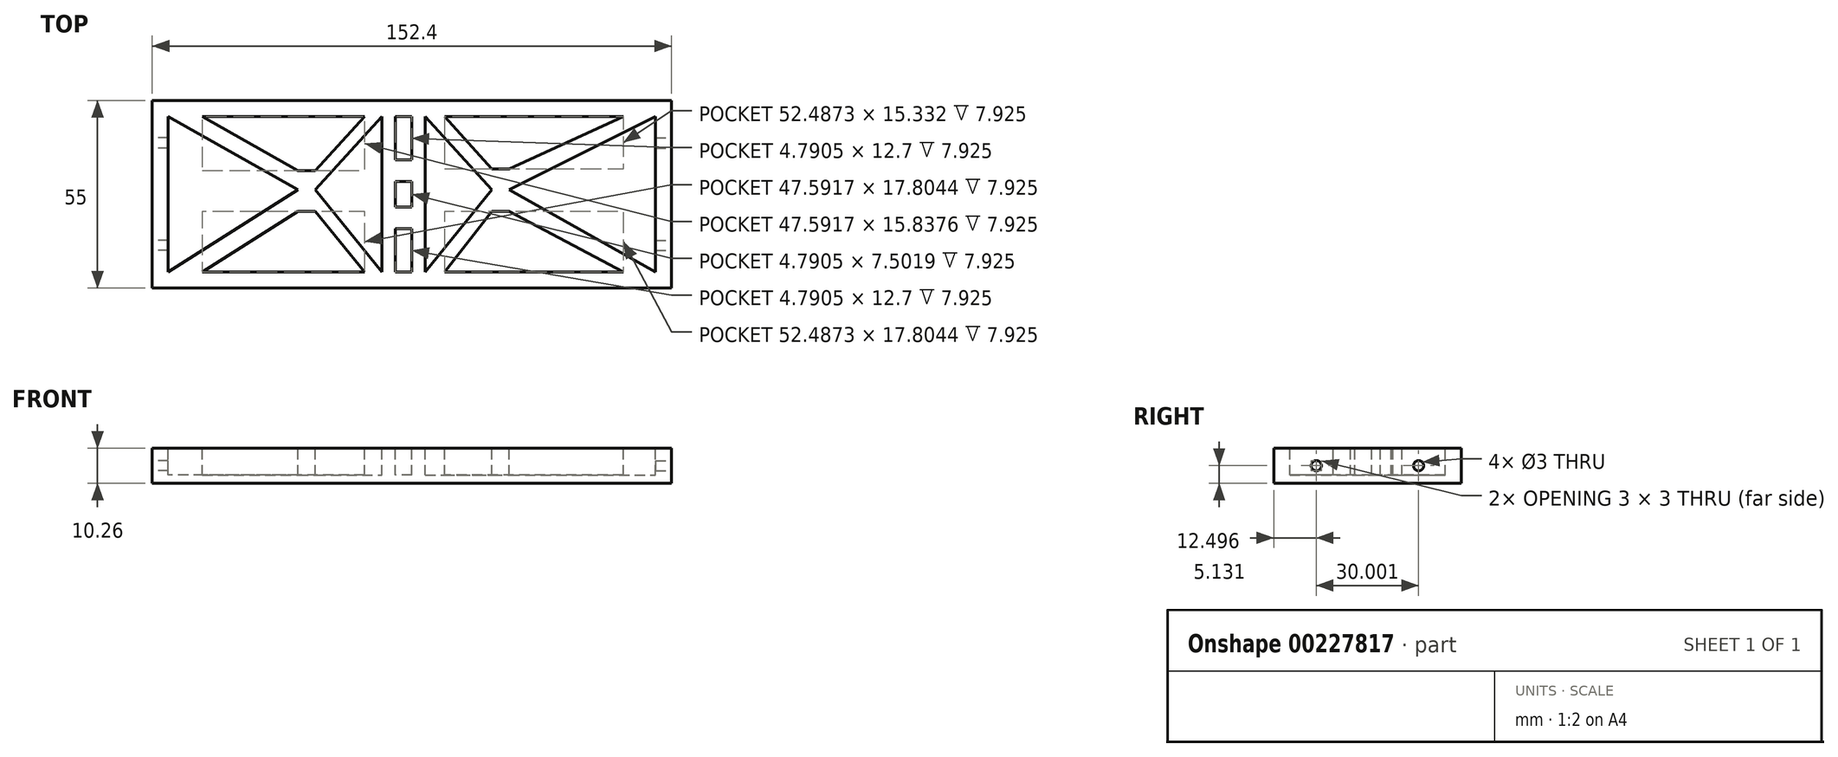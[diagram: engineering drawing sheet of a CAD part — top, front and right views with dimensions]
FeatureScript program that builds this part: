
annotation { "Feature Type Name" : "Feature", "Feature Type Description" : "" }
export const myFeature = defineFeature(function(context is Context, id is Id, definition is map)
    precondition{}
    {
        {
            var Q0;
            Q0=qCreatedBy(makeId("Top.planeOp"),FACE);
            var sketch = newSketch(context, id + "F0", { "sketchPlane" : qUnion([Q0])});
            skLineSegment(sketch, "E0.bottom", {"start": v(-61.95, 32.5) * mm, "end": v(90.45, 32.5) * mm});
            skLineSegment(sketch, "E0.top", {"start": v(-61.95, -22.5) * mm, "end": v(90.45, -22.5) * mm});
            skLineSegment(sketch, "E0.left", {"start": v(-61.95, 32.5) * mm, "end": v(-61.95, -22.5) * mm});
            skLineSegment(sketch, "E0.right", {"start": v(90.45, 32.5) * mm, "end": v(90.45, -22.5) * mm});
            skSolve(sketch);
        }
        {
            var Q0;
            Q0=makeQuery(id+"F0.imprint","IMPRINT",FACE,{"disambiguationData":[TD([[makeQuery(id+"F0.imprint","IMPRINT",EDGE,{"derivedFrom":sQuery(id+"F0.wireOp",EDGE,"E0.bottom")}),-1.0]])]});
            extrude(context, id + "F1", {"entities" : qUnion([Q0]), "depth" : 10.26 * mm});
        }
        {
            var Q0;
            Q0=makeQuery(id+"F1.opExtrude","CAP_FACE",FACE,{"disambiguationData":[OSD([sQuery(id+"F0.wireOp",EDGE,"E0.bottom"),sQuery(id+"F0.wireOp",EDGE,"E0.top"),sQuery(id+"F0.wireOp",EDGE,"E0.left"),sQuery(id+"F0.wireOp",EDGE,"E0.right")])],"isStart":false});
            var sketch = newSketch(context, id + "F2", { "sketchPlane" : qUnion([Q0])});
            skLineSegment(sketch, "E1", {"start": v(-57.25, -17.8) * mm, "end": v(-57.25, 27.8) * mm});
            skLineSegment(sketch, "E2", {"start": v(-57.25, 27.8) * mm, "end": v(-19.15, 6.28) * mm});
            skLineSegment(sketch, "E3", {"start": v(-19.15, 6.28) * mm, "end": v(-57.25, -17.8) * mm});
            skLineSegment(sketch, "E4", {"start": v(42.86, 6.28) * mm, "end": v(85.75, 27.8) * mm});
            skLineSegment(sketch, "E5", {"start": v(85.75, 27.8) * mm, "end": v(85.75, -17.8) * mm});
            skLineSegment(sketch, "E6", {"start": v(85.75, -17.8) * mm, "end": v(42.86, 6.28) * mm});
            skLineSegment(sketch, "E7", {"start": v(-14.07, 6.28) * mm, "end": v(5.5, 27.8) * mm});
            skLineSegment(sketch, "E8", {"start": v(5.5, 27.8) * mm, "end": v(5.5, -17.8) * mm});
            skLineSegment(sketch, "E9", {"start": v(5.5, -17.8) * mm, "end": v(-14.07, 6.28) * mm});
            skLineSegment(sketch, "E10", {"start": v(37.78, 6.28) * mm, "end": v(18.2, 27.8) * mm});
            skLineSegment(sketch, "E11", {"start": v(18.2, 27.8) * mm, "end": v(18.2, -17.8) * mm});
            skLineSegment(sketch, "E12", {"start": v(18.2, -17.8) * mm, "end": v(37.78, 6.28) * mm});
            skLineSegment(sketch, "E13", {"start": v(-47.2, -17.8) * mm, "end": v(-19.15, 0) * mm});
            skLineSegment(sketch, "E14", {"start": v(-19.15, 0) * mm, "end": v(-14.07, 0) * mm});
            skLineSegment(sketch, "E15", {"start": v(-14.07, 0) * mm, "end": v(0.4, -17.8) * mm});
            skLineSegment(sketch, "E16", {"start": v(0.4, -17.8) * mm, "end": v(-47.2, -17.8) * mm});
            skLineSegment(sketch, "E17", {"start": v(-47.2, 27.8) * mm, "end": v(-19.15, 11.96) * mm});
            skLineSegment(sketch, "E18", {"start": v(-19.15, 11.96) * mm, "end": v(-14.07, 11.96) * mm});
            skLineSegment(sketch, "E19", {"start": v(-14.07, 11.96) * mm, "end": v(0.4, 27.8) * mm});
            skLineSegment(sketch, "E20", {"start": v(0.4, 27.8) * mm, "end": v(-47.2, 27.8) * mm});
            skLineSegment(sketch, "E21", {"start": v(76.31, -17.8) * mm, "end": v(42.86, 0) * mm});
            skLineSegment(sketch, "E22", {"start": v(42.86, 0) * mm, "end": v(37.78, 0) * mm});
            skLineSegment(sketch, "E23", {"start": v(37.78, 0) * mm, "end": v(23.83, -17.8) * mm});
            skLineSegment(sketch, "E24", {"start": v(23.83, -17.8) * mm, "end": v(76.31, -17.8) * mm});
            skLineSegment(sketch, "E25", {"start": v(76.31, 27.8) * mm, "end": v(23.83, 27.8) * mm});
            skLineSegment(sketch, "E26", {"start": v(23.83, 27.8) * mm, "end": v(37.78, 12.47) * mm});
            skLineSegment(sketch, "E27", {"start": v(37.78, 12.47) * mm, "end": v(42.86, 12.47) * mm});
            skLineSegment(sketch, "E28", {"start": v(42.86, 12.47) * mm, "end": v(76.31, 27.8) * mm});
            skLineSegment(sketch, "E29.bottom", {"start": v(14.24, 27.8) * mm, "end": v(9.45, 27.8) * mm});
            skLineSegment(sketch, "E29.top", {"start": v(14.24, 15.1) * mm, "end": v(9.45, 15.1) * mm});
            skLineSegment(sketch, "E29.left", {"start": v(14.24, 27.8) * mm, "end": v(14.24, 15.1) * mm});
            skLineSegment(sketch, "E29.right", {"start": v(9.45, 27.8) * mm, "end": v(9.45, 15.1) * mm});
            skLineSegment(sketch, "E30.bottom", {"start": v(9.45, -5.1) * mm, "end": v(14.24, -5.1) * mm});
            skLineSegment(sketch, "E30.top", {"start": v(9.45, -17.8) * mm, "end": v(14.24, -17.8) * mm});
            skLineSegment(sketch, "E30.left", {"start": v(9.45, -5.1) * mm, "end": v(9.45, -17.8) * mm});
            skLineSegment(sketch, "E30.right", {"start": v(14.24, -5.1) * mm, "end": v(14.24, -17.8) * mm});
            skLineSegment(sketch, "E31.bottom", {"start": v(9.45, 1.25) * mm, "end": v(14.24, 1.25) * mm});
            skLineSegment(sketch, "E31.top", {"start": v(9.45, 8.75) * mm, "end": v(14.24, 8.75) * mm});
            skLineSegment(sketch, "E31.left", {"start": v(9.45, 1.25) * mm, "end": v(9.45, 8.75) * mm});
            skLineSegment(sketch, "E31.right", {"start": v(14.24, 1.25) * mm, "end": v(14.24, 8.75) * mm});
            skSolve(sketch);
        }
        {
            var Q0;
            Q0=makeQuery(id+"F2.imprint","IMPRINT",FACE,{"disambiguationData":[TD([[makeQuery(id+"F2.imprint","IMPRINT",EDGE,{"derivedFrom":sQuery(id+"F2.wireOp",EDGE,"E1")}),-1.0]])]});
            var Q1;
            Q1=makeQuery(id+"F2.imprint","IMPRINT",FACE,{"disambiguationData":[TD([[makeQuery(id+"F2.imprint","IMPRINT",EDGE,{"derivedFrom":sQuery(id+"F2.wireOp",EDGE,"E17")}),1.0]])]});
            var Q2;
            Q2=makeQuery(id+"F2.imprint","IMPRINT",FACE,{"disambiguationData":[TD([[makeQuery(id+"F2.imprint","IMPRINT",EDGE,{"derivedFrom":sQuery(id+"F2.wireOp",EDGE,"E13")}),-1.0]])]});
            var Q3;
            Q3=makeQuery(id+"F2.imprint","IMPRINT",FACE,{"disambiguationData":[TD([[makeQuery(id+"F2.imprint","IMPRINT",EDGE,{"derivedFrom":sQuery(id+"F2.wireOp",EDGE,"E7")}),-1.0]])]});
            var Q4;
            Q4=makeQuery(id+"F2.imprint","IMPRINT",FACE,{"disambiguationData":[TD([[makeQuery(id+"F2.imprint","IMPRINT",EDGE,{"derivedFrom":sQuery(id+"F2.wireOp",EDGE,"E29.bottom")}),1.0]])]});
            var Q5;
            Q5=makeQuery(id+"F2.imprint","IMPRINT",FACE,{"disambiguationData":[TD([[makeQuery(id+"F2.imprint","IMPRINT",EDGE,{"derivedFrom":sQuery(id+"F2.wireOp",EDGE,"E31.bottom")}),1.0]])]});
            var Q6;
            Q6=makeQuery(id+"F2.imprint","IMPRINT",FACE,{"disambiguationData":[TD([[makeQuery(id+"F2.imprint","IMPRINT",EDGE,{"derivedFrom":sQuery(id+"F2.wireOp",EDGE,"E30.bottom")}),-1.0]])]});
            var Q7;
            Q7=makeQuery(id+"F2.imprint","IMPRINT",FACE,{"disambiguationData":[TD([[makeQuery(id+"F2.imprint","IMPRINT",EDGE,{"derivedFrom":sQuery(id+"F2.wireOp",EDGE,"E10")}),1.0]])]});
            var Q8;
            Q8=makeQuery(id+"F2.imprint","IMPRINT",FACE,{"disambiguationData":[TD([[makeQuery(id+"F2.imprint","IMPRINT",EDGE,{"derivedFrom":sQuery(id+"F2.wireOp",EDGE,"E21")}),1.0]])]});
            var Q9;
            Q9=makeQuery(id+"F2.imprint","IMPRINT",FACE,{"disambiguationData":[TD([[makeQuery(id+"F2.imprint","IMPRINT",EDGE,{"derivedFrom":sQuery(id+"F2.wireOp",EDGE,"E4")}),-1.0]])]});
            var Q10;
            Q10=makeQuery(id+"F2.imprint","IMPRINT",FACE,{"disambiguationData":[TD([[makeQuery(id+"F2.imprint","IMPRINT",EDGE,{"derivedFrom":sQuery(id+"F2.wireOp",EDGE,"E25")}),1.0]])]});
            extrude(context, id + "F3", {"entities" : qUnion([Q0, Q1, Q2, Q3, Q4, Q5, Q6, Q7, Q8, Q9, Q10]), "operationType" : NewBodyOperationType.REMOVE, "oppositeDirection" : true, "depth" : 7.92 * mm});
        }
        {
            var Q0;
            Q0=makeQuery(id+"F1.opExtrude","SWEPT_FACE",FACE,{"disambiguationData":[OSD([sQuery(id+"F0.wireOp",EDGE,"E0.left")])]});
            var sketch = newSketch(context, id + "F4", { "sketchPlane" : qUnion([Q0])});
            skCircle(sketch, "E32", {"center": v(-20, 5.13) * mm, "radius": 1.5 * mm});
            skPoint(sketch, "E32.centerSnap0", {"position": v(-32.5, 5.13) * mm});
            skCircle(sketch, "E33", {"center": v(10, 5.13) * mm, "radius": 1.5 * mm});
            skPoint(sketch, "E33.centerSnap0", {"position": v(22.5, 5.13) * mm});
            skSolve(sketch);
        }
        {
            var Q0;
            Q0=makeQuery(id+"F1.opExtrude","SWEPT_FACE",FACE,{"disambiguationData":[OSD([sQuery(id+"F0.wireOp",EDGE,"E0.right")])]});
            var sketch = newSketch(context, id + "F5", { "sketchPlane" : qUnion([Q0])});
            skCircle(sketch, "E34", {"center": v(20, 5.13) * mm, "radius": 1.5 * mm});
            skPoint(sketch, "E34.centerSnap0", {"position": v(32.5, 5.13) * mm});
            skCircle(sketch, "E35", {"center": v(-10, 5.13) * mm, "radius": 1.5 * mm});
            skPoint(sketch, "E35.centerSnap0", {"position": v(-22.5, 5.13) * mm});
            skSolve(sketch);
        }
        {
            var Q0;
            Q0=makeQuery(id+"F5.imprint","IMPRINT",FACE,{"disambiguationData":[TD([[makeQuery(id+"F5.imprint","IMPRINT",EDGE,{"derivedFrom":sQuery(id+"F5.wireOp",EDGE,"E34")}),1.0]])]});
            var Q1;
            Q1=makeQuery(id+"F5.imprint","IMPRINT",FACE,{"disambiguationData":[TD([[makeQuery(id+"F5.imprint","IMPRINT",EDGE,{"derivedFrom":sQuery(id+"F5.wireOp",EDGE,"E35")}),1.0]])]});
            extrude(context, id + "F6", {"entities" : qUnion([Q0, Q1]), "operationType" : NewBodyOperationType.REMOVE, "oppositeDirection" : true, "depth" : 6.35 * mm});
        }
        {
            var Q0;
            Q0=makeQuery(id+"F4.imprint","IMPRINT",FACE,{"disambiguationData":[TD([[makeQuery(id+"F4.imprint","IMPRINT",EDGE,{"derivedFrom":sQuery(id+"F4.wireOp",EDGE,"E32")}),1.0]])]});
            var Q1;
            Q1=makeQuery(id+"F4.imprint","IMPRINT",FACE,{"disambiguationData":[TD([[makeQuery(id+"F4.imprint","IMPRINT",EDGE,{"derivedFrom":sQuery(id+"F4.wireOp",EDGE,"E33")}),1.0]])]});
            extrude(context, id + "F7", {"entities" : qUnion([Q0, Q1]), "operationType" : NewBodyOperationType.REMOVE, "oppositeDirection" : true, "depth" : 6.35 * mm});
        }
    });
